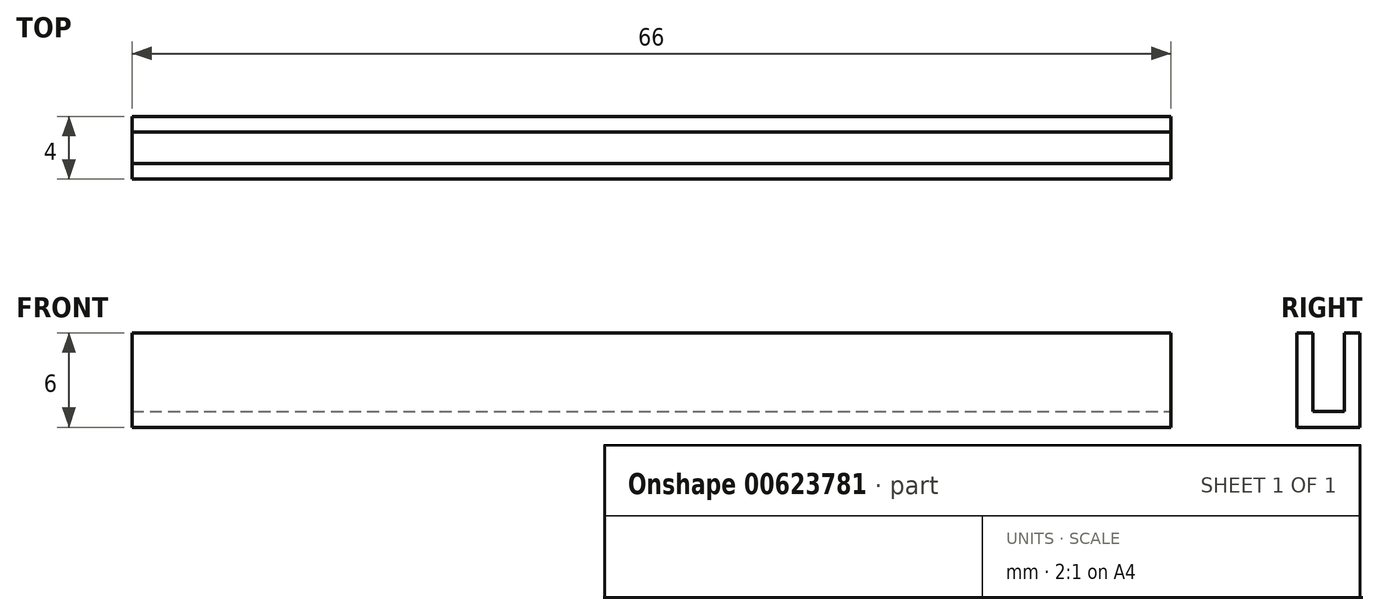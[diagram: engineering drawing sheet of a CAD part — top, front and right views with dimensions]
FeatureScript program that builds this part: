
annotation { "Feature Type Name" : "Feature", "Feature Type Description" : "" }
export const myFeature = defineFeature(function(context is Context, id is Id, definition is map)
    precondition{}
    {
        {
            var Q0;
            Q0=qCreatedBy(makeId("Top.planeOp"),FACE);
            var sketch = newSketch(context, id + "F0", { "sketchPlane" : qUnion([Q0])});
            skLineSegment(sketch, "E0.bottom", {"start": v(-33, 2) * mm, "end": v(33, 2) * mm});
            skLineSegment(sketch, "E0.top", {"start": v(-33, -2) * mm, "end": v(33, -2) * mm});
            skLineSegment(sketch, "E0.left", {"start": v(-33, 2) * mm, "end": v(-33, -2) * mm});
            skLineSegment(sketch, "E0.right", {"start": v(33, 2) * mm, "end": v(33, -2) * mm});
            skPoint(sketch, "E0.middle", {"position": v(0, 0) * mm});
            skSolve(sketch);
        }
        {
            var Q0;
            Q0=makeQuery(id+"F0.imprint","IMPRINT",FACE,{"disambiguationData":[TD([[makeQuery(id+"F0.imprint","IMPRINT",EDGE,{"derivedFrom":sQuery(id+"F0.wireOp",EDGE,"E0.bottom")}),-1.0]])]});
            extrude(context, id + "F1", {"entities" : qUnion([Q0]), "depth" : 1 * mm, "offsetDistance" : 25 * mm});
        }
        {
            var Q0;
            Q0=makeQuery(id+"F1.opExtrude","CAP_FACE",FACE,{"disambiguationData":[OSD([sQuery(id+"F0.wireOp",EDGE,"E0.bottom"),sQuery(id+"F0.wireOp",EDGE,"E0.top"),sQuery(id+"F0.wireOp",EDGE,"E0.left"),sQuery(id+"F0.wireOp",EDGE,"E0.right")])],"isStart":false});
            var sketch = newSketch(context, id + "F2", { "sketchPlane" : qUnion([Q0])});
            skLineSegment(sketch, "E1.bottom", {"start": v(-33, -2) * mm, "end": v(33, -2) * mm});
            skLineSegment(sketch, "E1.top", {"start": v(-33, -1) * mm, "end": v(33, -1) * mm});
            skLineSegment(sketch, "E1.left", {"start": v(-33, -2) * mm, "end": v(-33, -1) * mm});
            skLineSegment(sketch, "E1.right", {"start": v(33, -2) * mm, "end": v(33, -1) * mm});
            skLineSegment(sketch, "E2.bottom", {"start": v(-33, 2) * mm, "end": v(33, 2) * mm});
            skLineSegment(sketch, "E2.top", {"start": v(-33, 1) * mm, "end": v(33, 1) * mm});
            skLineSegment(sketch, "E2.left", {"start": v(-33, 2) * mm, "end": v(-33, 1) * mm});
            skLineSegment(sketch, "E2.right", {"start": v(33, 2) * mm, "end": v(33, 1) * mm});
            skSolve(sketch);
        }
        {
            var Q0;
            Q0=makeQuery(id+"F2.imprint","IMPRINT",FACE,{"disambiguationData":[TD([[makeQuery(id+"F2.imprint","IMPRINT",EDGE,{"derivedFrom":sQuery(id+"F2.wireOp",EDGE,"E2.bottom")}),-1.0]])]});
            var Q1;
            Q1=makeQuery(id+"F2.imprint","IMPRINT",FACE,{"disambiguationData":[TD([[makeQuery(id+"F2.imprint","IMPRINT",EDGE,{"derivedFrom":sQuery(id+"F2.wireOp",EDGE,"E1.bottom")}),1.0]])]});
            extrude(context, id + "F3", {"entities" : qUnion([Q0, Q1]), "operationType" : NewBodyOperationType.ADD, "depth" : 5 * mm, "offsetDistance" : 25 * mm});
        }
    });
